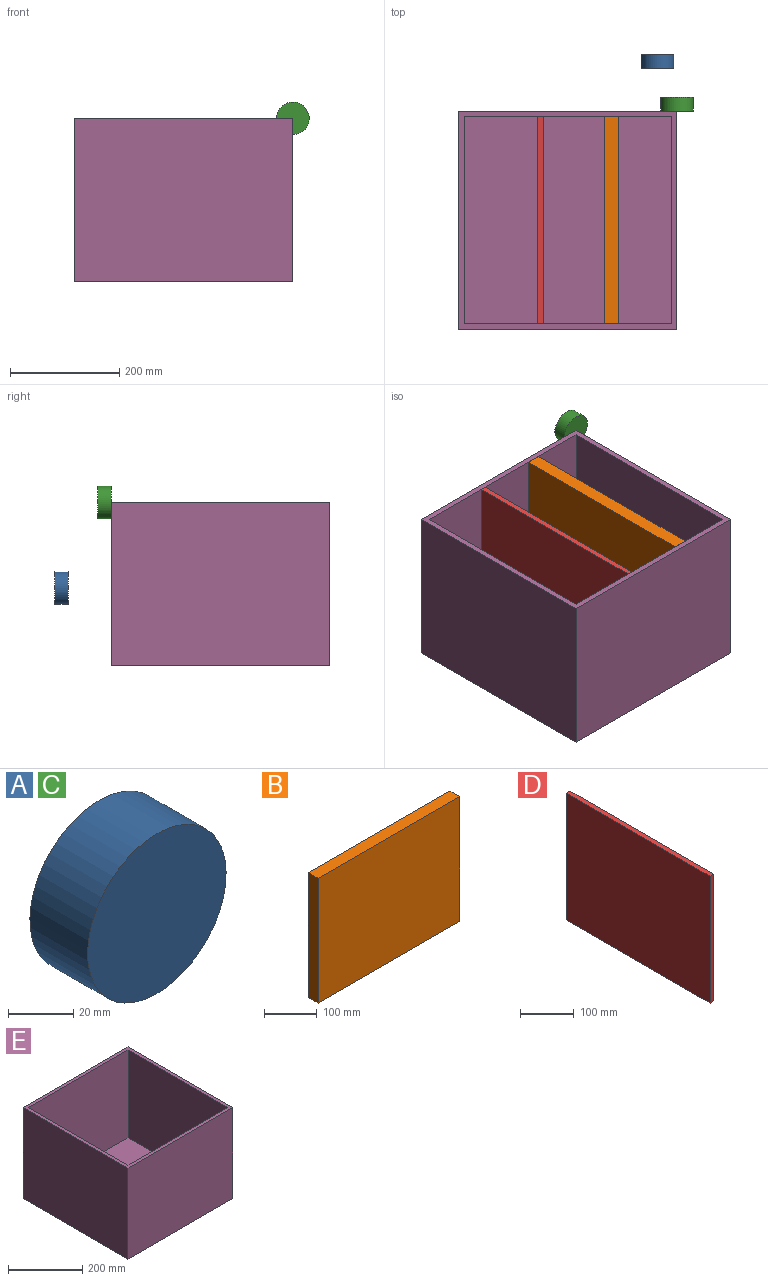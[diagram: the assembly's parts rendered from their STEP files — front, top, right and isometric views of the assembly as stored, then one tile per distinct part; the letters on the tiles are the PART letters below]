
ASSEMBLY  parts=5 mates=3
PART A: 3 faces, bbox 59.9x25x59.9 mm
  f0: cylinder r=29.97mm len=59.94mm, axis (0,-1,0), area 4707.5mm2, adj f1,f2
  f1: plane 59.94x59.94mm, normal (0,1,0), area 2821.6mm2, adj f0
  f2: plane 59.94x59.94mm, normal (0,-1,0), area 2821.6mm2, adj f0
PART B: 6 faces, bbox 380x26x290 mm
  f0: plane 380x26mm, normal (0,0,1), area 9880mm2, adj f1,f3,f4,f5
  f1: plane 290x26mm, normal (-1,0,0), area 7540mm2, adj f0,f2,f4,f5
  f2: plane 380x26mm, normal (0,0,-1), area 9880mm2, adj f1,f3,f4,f5
  f3: plane 290x26mm, normal (1,0,0), area 7540mm2, adj f0,f2,f4,f5
  f4: plane 380x290mm, normal (0,-1,0), area 110200mm2, adj f0,f1,f2,f3
  f5: plane 380x290mm, normal (0,1,0), area 110200mm2, adj f0,f1,f2,f3
PART C: same geometry as A
PART D: 6 faces, bbox 10x380x290 mm
  f0: plane 380x10mm, normal (0,0,1), area 3800mm2, adj f1,f3,f4,f5
  f1: plane 290x10mm, normal (0,-1,0), area 2900mm2, adj f0,f2,f4,f5
  f2: plane 380x10mm, normal (0,0,-1), area 3800mm2, adj f1,f3,f4,f5
  f3: plane 290x10mm, normal (0,1,0), area 2900mm2, adj f0,f2,f4,f5
  f4: plane 380x290mm, normal (1,0,0), area 110200mm2, adj f0,f1,f2,f3
  f5: plane 380x290mm, normal (-1,0,0), area 110200mm2, adj f0,f1,f2,f3
PART E: 11 faces, bbox 400x400x300 mm
  f0: plane 400x400mm, normal (0,0,1), area 15600mm2, adj f1,f3,f4,f5,f6,f8,f9,f10
  f1: plane 400x300mm, normal (-1,0,0), area 120000mm2, adj f0,f2,f4,f5
  f2: plane 400x400mm, normal (0,0,-1), area 160000mm2, adj f1,f3,f4,f5
  f3: plane 400x300mm, normal (1,0,0), area 120000mm2, adj f0,f2,f4,f5
  f4: plane 400x300mm, normal (0,-1,0), area 120000mm2, adj f0,f1,f2,f3
  f5: plane 400x300mm, normal (0,1,0), area 120000mm2, adj f0,f1,f2,f3
  f6: plane 380x290mm, normal (1,0,0), area 110200mm2, adj f0,f7,f9,f10
  f7: plane 380x380mm, normal (0,0,1), area 144400mm2, adj f6,f8,f9,f10
  f8: plane 380x290mm, normal (-1,0,0), area 110200mm2, adj f0,f7,f9,f10
  f9: plane 380x290mm, normal (0,1,0), area 110200mm2, adj f0,f6,f7,f8
  f10: plane 380x290mm, normal (0,-1,0), area 110200mm2, adj f0,f6,f7,f8
PLACE A t=(62.16,290.75,-21.04)mm
PLACE B rot(axis=(0,0,1),90deg) t=(-319,0,0)mm
PLACE C t=(97.42,212,136.12)mm
PLACE D rot(axis=(0,1,0),180deg) t=(-396,-585.51,135.21)mm
PLACE E at identity fixed
MATE fastened C.f0 <-> E.f5  axis (0,-1,0) through (0,0,300)mm
MATE fastened B.f3 <-> E.f10  axis (0,1,0) through (-120,-10,155)mm
MATE fastened D.f1 <-> E.f9  axis (0,-1,0) through (-250,-390,155)mm
